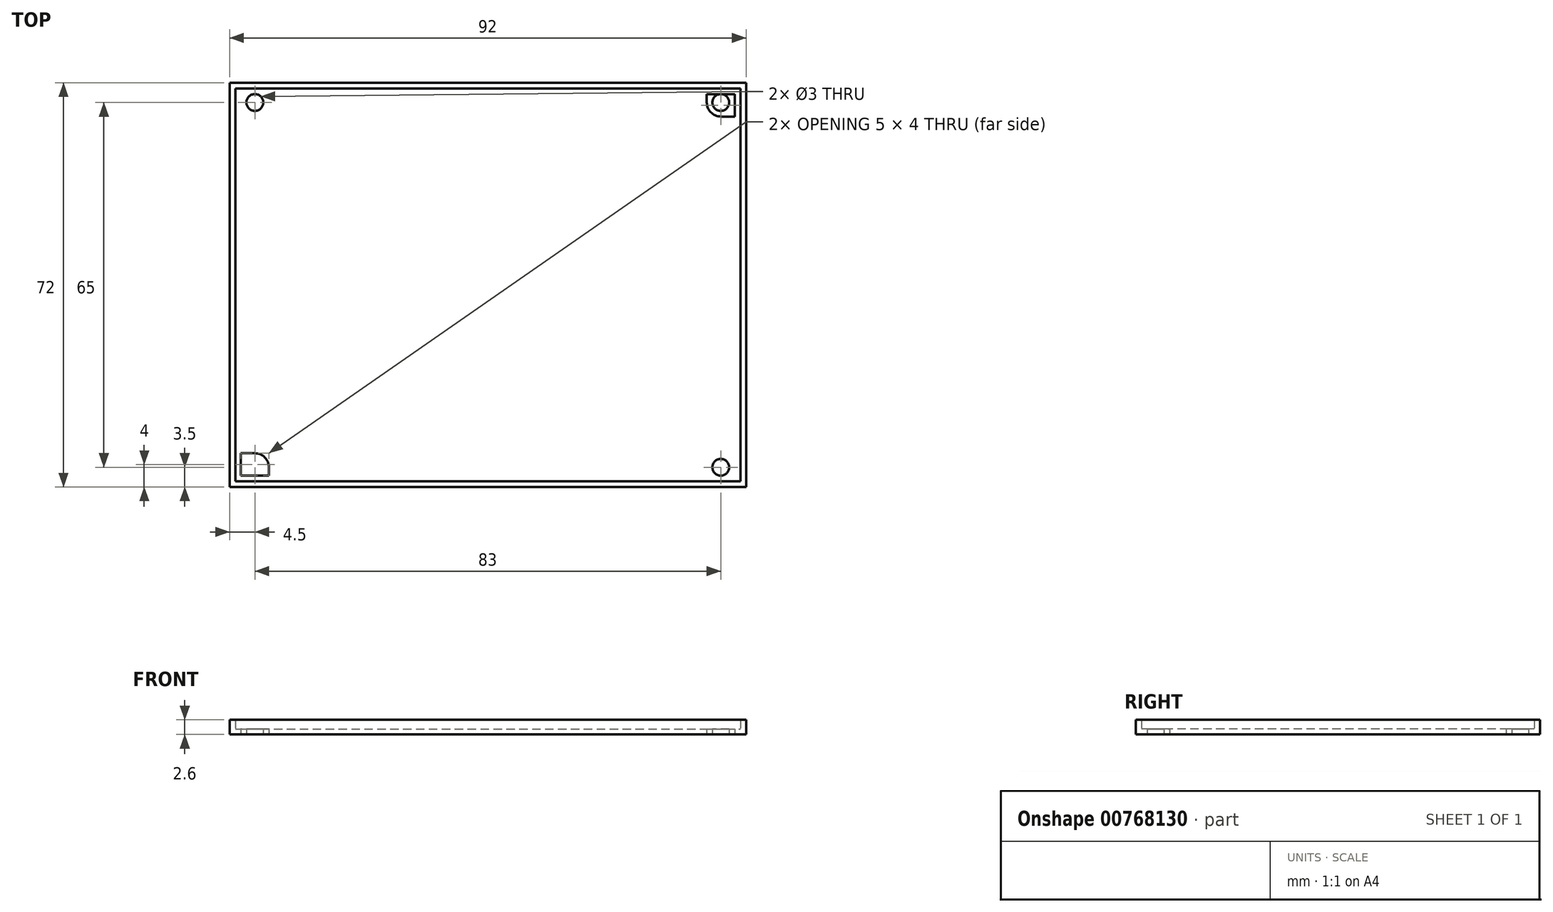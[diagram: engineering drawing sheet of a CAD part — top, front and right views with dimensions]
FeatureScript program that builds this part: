
annotation { "Feature Type Name" : "Feature", "Feature Type Description" : "" }
export const myFeature = defineFeature(function(context is Context, id is Id, definition is map)
    precondition{}
    {
        {
            var Q0;
            Q0=qCreatedBy(makeId("Top.planeOp"),FACE);
            var sketch = newSketch(context, id + "F0", { "sketchPlane" : qUnion([Q0])});
            skLineSegment(sketch, "E0.bottom", {"start": v(-45, 35) * mm, "end": v(45, 35) * mm, "construction": true});
            skLineSegment(sketch, "E0.top", {"start": v(-45, -35) * mm, "end": v(45, -35) * mm, "construction": true});
            skLineSegment(sketch, "E0.left", {"start": v(-45, 35) * mm, "end": v(-45, -35) * mm, "construction": true});
            skLineSegment(sketch, "E0.right", {"start": v(45, 35) * mm, "end": v(45, -35) * mm, "construction": true});
            skLineSegment(sketch, "E1.bottom", {"start": v(-46, 36) * mm, "end": v(46, 36) * mm});
            skLineSegment(sketch, "E1.top", {"start": v(-46, -36) * mm, "end": v(46, -36) * mm});
            skLineSegment(sketch, "E1.left", {"start": v(-46, 36) * mm, "end": v(-46, -36) * mm});
            skLineSegment(sketch, "E1.right", {"start": v(46, 36) * mm, "end": v(46, -36) * mm});
            skLineSegment(sketch, "E2.bottom", {"start": v(-44, 34) * mm, "end": v(44, 34) * mm});
            skLineSegment(sketch, "E2.top", {"start": v(-44, -34) * mm, "end": v(44, -34) * mm});
            skLineSegment(sketch, "E2.left", {"start": v(-44, 34) * mm, "end": v(-44, -34) * mm});
            skLineSegment(sketch, "E2.right", {"start": v(44, 34) * mm, "end": v(44, -34) * mm});
            skPoint(sketch, "E3", {"position": v(-41.5, 32.5) * mm});
            skCircle(sketch, "E4", {"center": v(-41.5, 32.5) * mm, "radius": 1.5 * mm});
            skArc(sketch, "E5", {"start": v(-41.5, 30) * mm, "mid": v(-39.73, 30.73) * mm, "end": v(-39, 32.5) * mm});
            skLineSegment(sketch, "E6", {"start": v(-39, 32.5) * mm, "end": v(-39, 34) * mm});
            skLineSegment(sketch, "E7", {"start": v(-41.5, 30) * mm, "end": v(-44, 30) * mm});
            skCircle(sketch, "E8.MirrorC", {"center": v(41.5, 32.5) * mm, "radius": 1.5 * mm});
            skLineSegment(sketch, "E9.MirrorCS", {"start": v(41.5, 30) * mm, "end": v(44, 30) * mm});
            skArc(sketch, "E10.MirrorCS", {"start": v(41.5, 30) * mm, "mid": v(39.73, 30.73) * mm, "end": v(39, 32.5) * mm});
            skLineSegment(sketch, "E11.MirrorCS", {"start": v(39, 32.5) * mm, "end": v(39, 34) * mm});
            skArc(sketch, "E12.MirrorCS", {"start": v(-41.5, -30) * mm, "mid": v(-39.73, -30.73) * mm, "end": v(-39, -32.5) * mm});
            skLineSegment(sketch, "E13.MirrorCS", {"start": v(-41.5, -30) * mm, "end": v(-44, -30) * mm});
            skCircle(sketch, "E14.MirrorC", {"center": v(-41.5, -32.5) * mm, "radius": 1.5 * mm});
            skLineSegment(sketch, "E15.MirrorCS", {"start": v(-39, -32.5) * mm, "end": v(-39, -34) * mm});
            skLineSegment(sketch, "E16.MirrorCS", {"start": v(39, -32.5) * mm, "end": v(39, -34) * mm});
            skArc(sketch, "E17.MirrorCS", {"start": v(41.5, -30) * mm, "mid": v(39.73, -30.73) * mm, "end": v(39, -32.5) * mm});
            skLineSegment(sketch, "E18.MirrorCS", {"start": v(41.5, -30) * mm, "end": v(44, -30) * mm});
            skCircle(sketch, "E19.MirrorC", {"center": v(41.5, -32.5) * mm, "radius": 1.5 * mm});
            skSolve(sketch);
        }
        {
            var Q0;
            Q0=makeQuery(id+"F0.imprint","IMPRINT",FACE,{"disambiguationData":[TD([[makeQuery(id+"F0.imprint","IMPRINT",EDGE,{"derivedFrom":sQuery(id+"F0.wireOp",EDGE,"E1.bottom")}),-1.0]])]});
            var Q1;
            Q1=makeQuery(id+"F0.imprint","IMPRINT",FACE,{"disambiguationData":[TD([[makeQuery(id+"F0.imprint","IMPRINT",EDGE,{"derivedFrom":sQuery(id+"F0.wireOp",EDGE,"E8.MirrorC")}),1.0]])]});
            var Q2;
            {var subQ0=sQuery(id+"F0.wireOp",EDGE,"E16.MirrorCS");Q2=makeQuery(id+"F0.imprint","IMPRINT",FACE,{"disambiguationData":[TD([[makeQuery(id+"F0.imprint","IMPRINT",EDGE,{"derivedFrom":subQ0}),1.0]])]});}
            var Q3;
            Q3=makeQuery(id+"F0.imprint","IMPRINT",FACE,{"disambiguationData":[TD([[makeQuery(id+"F0.imprint","IMPRINT",EDGE,{"derivedFrom":sQuery(id+"F0.wireOp",EDGE,"E12.MirrorCS")}),-1.0]])]});
            var Q4;
            Q4=makeQuery(id+"F0.imprint","IMPRINT",FACE,{"disambiguationData":[TD([[makeQuery(id+"F0.imprint","IMPRINT",EDGE,{"derivedFrom":sQuery(id+"F0.wireOp",EDGE,"E4")}),-1.0]])]});
            extrude(context, id + "F1", {"entities" : qUnion([Q0, Q1, Q2, Q3, Q4]), "depth" : 1 * mm, "offsetDistance" : 25 * mm});
        }
        {
            var Q0;
            Q0=makeQuery(id+"F1.opExtrude","CAP_FACE",FACE,{"disambiguationData":[OSD([sQuery(id+"F0.wireOp",EDGE,"E1.bottom"),sQuery(id+"F0.wireOp",EDGE,"E1.top"),sQuery(id+"F0.wireOp",EDGE,"E1.left"),sQuery(id+"F0.wireOp",EDGE,"E1.right"),sQuery(id+"F0.wireOp",EDGE,"E2.bottom"),sQuery(id+"F0.wireOp",EDGE,"E2.top"),sQuery(id+"F0.wireOp",EDGE,"E2.left"),sQuery(id+"F0.wireOp",EDGE,"E2.right")])],"isStart":false});
            var sketch = newSketch(context, id + "F2", { "sketchPlane" : qUnion([Q0])});
            skLineSegment(sketch, "E20.bottom", {"start": v(-45, 35) * mm, "end": v(45, 35) * mm});
            skLineSegment(sketch, "E20.top", {"start": v(-45, -35) * mm, "end": v(45, -35) * mm});
            skLineSegment(sketch, "E20.left", {"start": v(-45, 35) * mm, "end": v(-45, -35) * mm});
            skLineSegment(sketch, "E20.right", {"start": v(45, 35) * mm, "end": v(45, -35) * mm});
            skSolve(sketch);
        }
        {
            var Q0;
            Q0=makeQuery(id+"F2.imprint","IMPRINT",FACE,{"disambiguationData":[TD([[makeQuery(id+"F2.imprint","IMPRINT",EDGE,{"derivedFrom":sQuery(id+"F2.wireOp",EDGE,"E20.bottom")}),1.0]])]});
            extrude(context, id + "F3", {"entities" : qUnion([Q0]), "operationType" : NewBodyOperationType.ADD, "depth" : 1.6 * mm, "offsetDistance" : 25 * mm});
        }
    });
